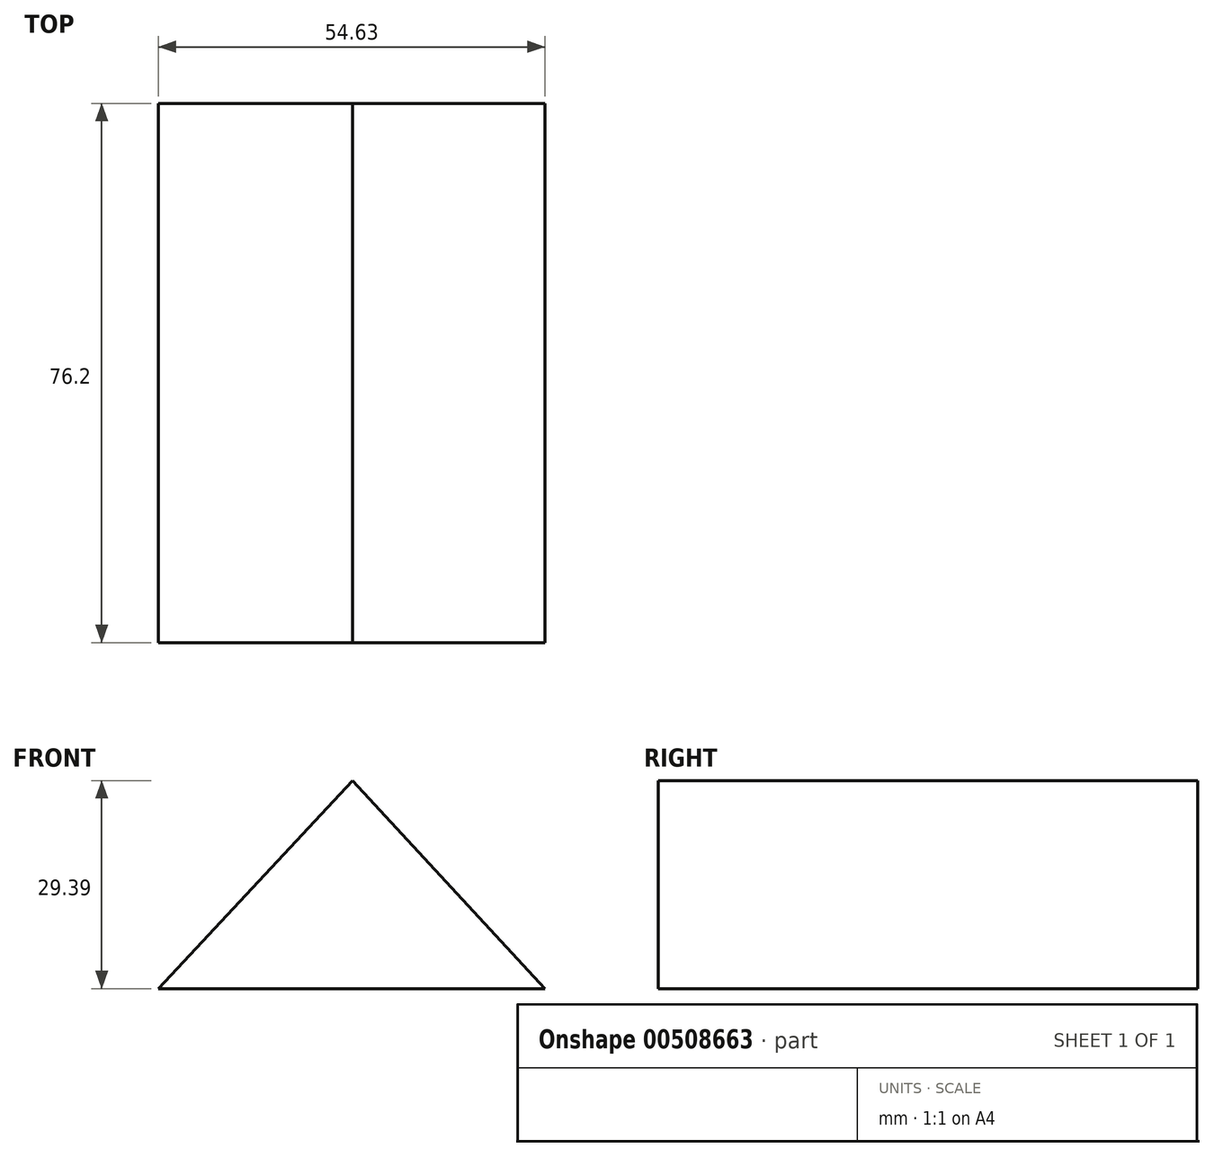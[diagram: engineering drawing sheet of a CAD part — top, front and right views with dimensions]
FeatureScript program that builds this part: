
annotation { "Feature Type Name" : "Feature", "Feature Type Description" : "" }
export const myFeature = defineFeature(function(context is Context, id is Id, definition is map)
    precondition{}
    {
        {
            var Q0;
            Q0=qCreatedBy(makeId("Front.planeOp"),FACE);
            var sketch = newSketch(context, id + "F0", { "sketchPlane" : qUnion([Q0])});
            skLineSegment(sketch, "E0", {"start": v(-27.42, 0) * mm, "end": v(27.2, 0) * mm});
            skLineSegment(sketch, "E1", {"start": v(-27.42, 0) * mm, "end": v(0, 29.4) * mm});
            skLineSegment(sketch, "E2", {"start": v(0, 29.4) * mm, "end": v(27.2, 0) * mm});
            skLineSegment(sketch, "E3", {"start": v(0, 29.39) * mm, "end": v(0, 0) * mm});
            skSolve(sketch);
        }
        {
            var Q0;
            Q0=qSketchRegion(id+"F0",true);
            extrude(context, id + "F1", {"entities" : qUnion([Q0]), "depth" : 76.2 * mm});
        }
    });
